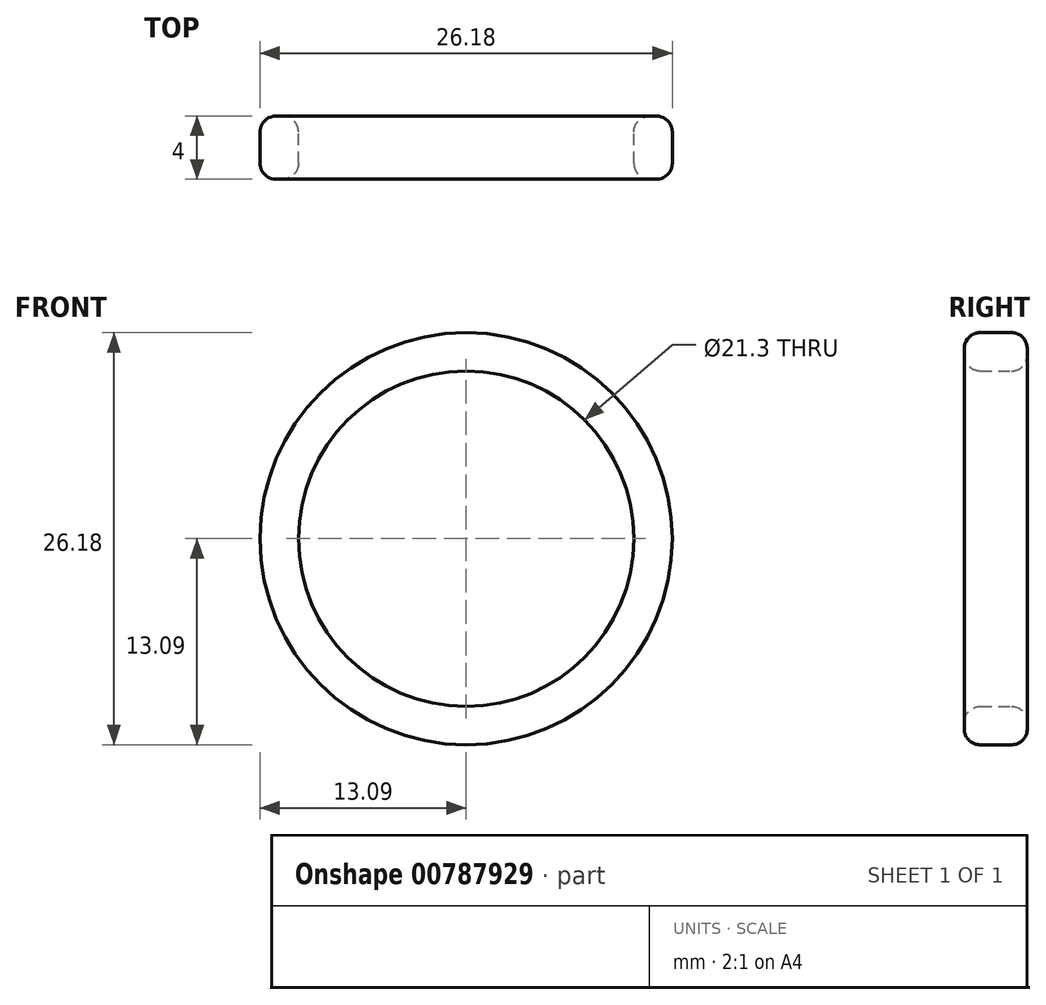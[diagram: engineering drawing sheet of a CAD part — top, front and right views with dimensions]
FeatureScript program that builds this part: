
annotation { "Feature Type Name" : "Feature", "Feature Type Description" : "" }
export const myFeature = defineFeature(function(context is Context, id is Id, definition is map)
    precondition{}
    {
        {
            var Q0;
            Q0=qCreatedBy(makeId("Front.planeOp"),FACE);
            var sketch = newSketch(context, id + "F0", { "sketchPlane" : qUnion([Q0])});
            skCircle(sketch, "E0", {"center": v(0, 0) * mm, "radius": 10.65 * mm});
            skCircle(sketch, "E1.0", {"center": v(0, 0) * mm, "radius": 13.09 * mm});
            skSolve(sketch);
        }
        {
            var Q0;
            Q0 = qSketchRegion(id + "F0", true);
            extrude(context, id + "F1", {"entities" : qUnion([Q0]), "depth" : 4 * mm, "offsetDistance" : 25 * mm});
        }
        {
            var Q0;
            Q0=makeQuery(id+"F1.opExtrude","CAP_EDGE",EDGE,{"disambiguationData":[OSD([sQuery(id+"F0.wireOp",EDGE,"E1.0")])],"isStart":false});
            var Q1;
            Q1=makeQuery(id+"F1.opExtrude","CAP_EDGE",EDGE,{"disambiguationData":[OSD([sQuery(id+"F0.wireOp",EDGE,"E1.0")])],"isStart":true});
            var Q2;
            Q2=makeQuery(id+"F1.opExtrude","CAP_EDGE",EDGE,{"disambiguationData":[OSD([sQuery(id+"F0.wireOp",EDGE,"E0")])],"isStart":false});
            var Q3;
            Q3=makeQuery(id+"F1.opExtrude","CAP_EDGE",EDGE,{"disambiguationData":[OSD([sQuery(id+"F0.wireOp",EDGE,"E0")])],"isStart":true});
            fillet(context, id + "F2", {"entities" : qUnion([Q0, Q1, Q2, Q3]), "radius" : 1 * mm, "tangentPropagation" : true, "allowEdgeOverflow" : false});
        }
    });
